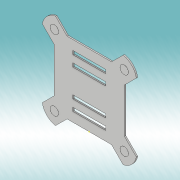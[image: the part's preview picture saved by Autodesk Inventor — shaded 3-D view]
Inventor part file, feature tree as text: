
AUTODESK INVENTOR PART (.ipt)
format: ipt  version: 2019 (Build 230136000, 136)  size: 177,664 bytes
history: native  units: mm
features: sketch x3, extrude x3
ambient origin geometry x8: Origin, YZ Plane, XZ Plane, XY Plane, X Axis, Y Axis, Z Axis, Center Point
bodies: Solid1 (feature_tree)
feature tree (6):
  sketch  "Sketch1"  dims[d0=135.0deg d1=47.5mm]
  extrude  "Extrusion1"  Depth=47.5mm
  extrude  "Extrusion2"  Depth=40.0mm
  sketch  "Sketch2"  dims[d2=35.0mm d3=40.0mm]
  extrude  "Extrusion3"  Depth=35.0mm
  sketch  "Sketch3"  dims[d4=75.0mm d5=35.0mm d6=66.0mm d7=1.5mm d8=1.5mm d9=0.0mm d10=0.0mm d11=20.0mm d12=38.0mm d13=18.0mm d14=3.2mm d15=0.0mm d21=35.0mm d22=8.0mm d23=150.0mm d24=15.0mm d25=20.0mm d26=10.0mm d27=0.0mm]
